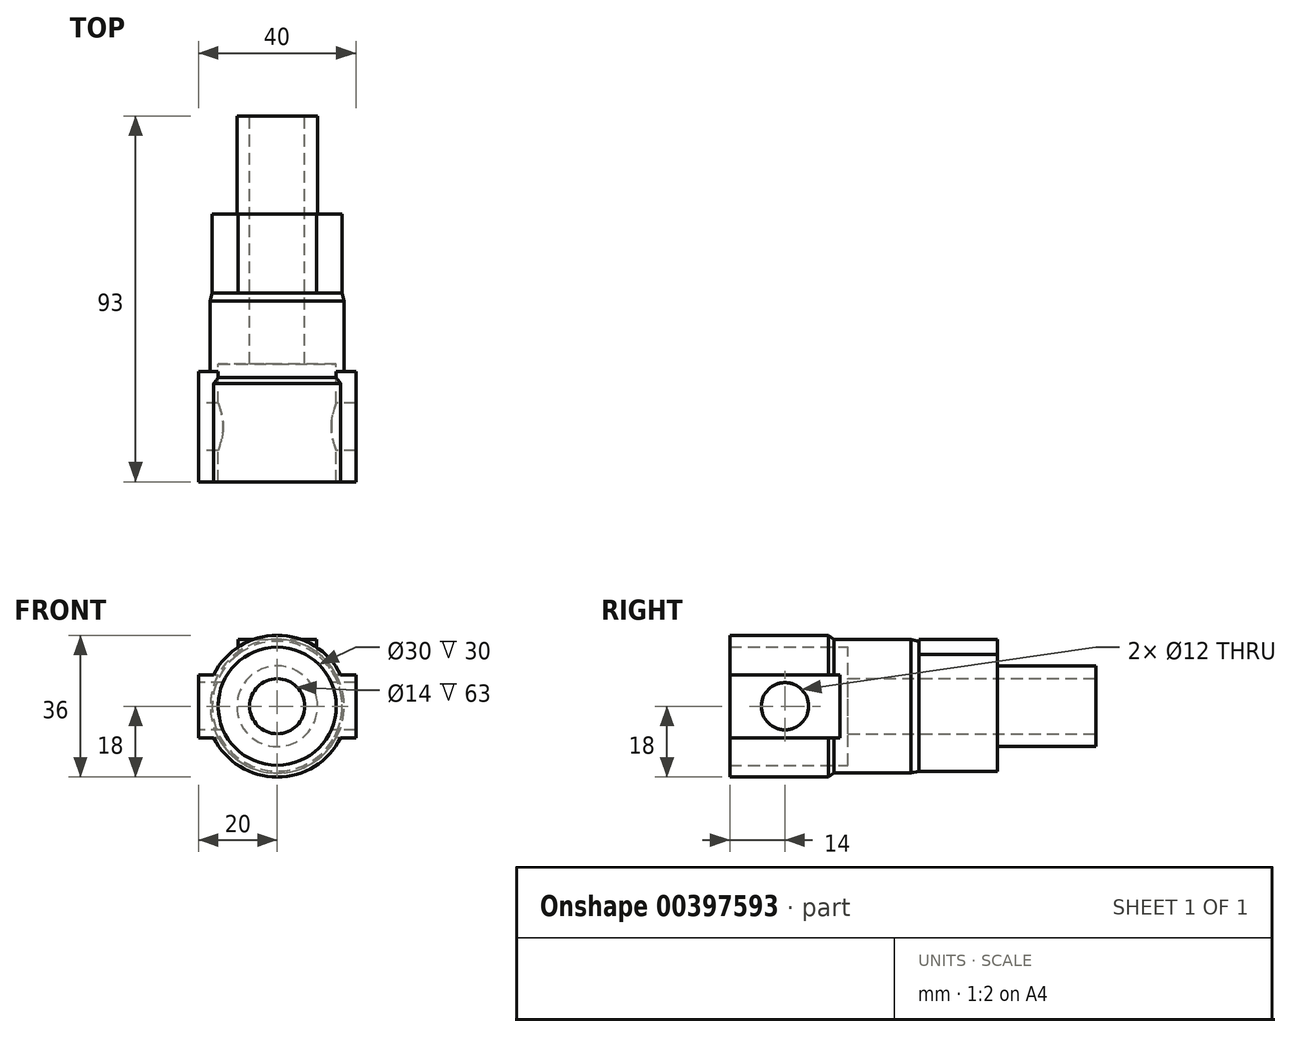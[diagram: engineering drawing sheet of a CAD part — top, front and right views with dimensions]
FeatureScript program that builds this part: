
annotation { "Feature Type Name" : "Feature", "Feature Type Description" : "" }
export const myFeature = defineFeature(function(context is Context, id is Id, definition is map)
    precondition{}
    {
        {
            var Q0;
            Q0=qCreatedBy(makeId("Front.planeOp"),FACE);
            var sketch = newSketch(context, id + "F0", { "sketchPlane" : qUnion([Q0])});
            skCircle(sketch, "E0", {"center": v(0, 0) * mm, "radius": 15 * mm});
            skCircle(sketch, "E1", {"center": v(0, 0) * mm, "radius": 18 * mm});
            skSolve(sketch);
        }
        {
            var Q0;
            Q0=qSketchRegion(id+"F0",true);
            extrude(context, id + "F1", {"entities" : qUnion([Q0]), "depth" : 28 * mm});
        }
        {
            var Q0;
            Q0=qCreatedBy(makeId("Right.planeOp"),FACE);
            var sketch = newSketch(context, id + "F2", { "sketchPlane" : qUnion([Q0])});
            skLineSegment(sketch, "E2", {"start": v(0, 0) * mm, "end": v(0, 8) * mm});
            skLineSegment(sketch, "E3", {"start": v(0, 0) * mm, "end": v(0, -8) * mm});
            skLineSegment(sketch, "E4.bottom", {"start": v(0, 8) * mm, "end": v(-28, 8) * mm});
            skLineSegment(sketch, "E4.top", {"start": v(0, -8) * mm, "end": v(-28, -8) * mm});
            skLineSegment(sketch, "E4.left", {"start": v(0, 8) * mm, "end": v(0, -8) * mm});
            skLineSegment(sketch, "E4.right", {"start": v(-28, 8) * mm, "end": v(-28, -8) * mm});
            skSolve(sketch);
        }
        {
            var Q0;
            Q0=qSketchRegion(id+"F2",true);
            extrude(context, id + "F3", {"entities" : qUnion([Q0]), "operationType" : NewBodyOperationType.ADD, "oppositeDirection" : true, "depth" : 20 * mm});
        }
        {
            var Q0;
            Q0=makeQuery(id+"F3.opExtrude","CAP_FACE",FACE,{"disambiguationData":[OSD([sQuery(id+"F2.wireOp",EDGE,"E4.bottom"),sQuery(id+"F2.wireOp",EDGE,"E4.top"),sQuery(id+"F2.wireOp",EDGE,"E4.left"),sQuery(id+"F2.wireOp",EDGE,"E4.right")])],"isStart":true});
            extrude(context, id + "F4", {"entities" : qUnion([Q0]), "operationType" : NewBodyOperationType.ADD, "depth" : 20 * mm});
        }
        {
            var Q0;
            Q0=makeQuery(id+"F1.opExtrude","CAP_FACE",FACE,{"disambiguationData":[OSD([sQuery(id+"F0.wireOp",EDGE,"E0"),sQuery(id+"F0.wireOp",EDGE,"E1")])],"isStart":false});
            var sketch = newSketch(context, id + "F5", { "sketchPlane" : qUnion([Q0])});
            skCircle(sketch, "E5", {"center": v(0, 0) * mm, "radius": 9 * mm});
            skSolve(sketch);
        }
        {
            var Q0;
            Q0=qSketchRegion(id+"F5",true);
            extrude(context, id + "F6", {"entities" : qUnion([Q0]), "operationType" : NewBodyOperationType.REMOVE, "oppositeDirection" : true, "depth" : 25 * mm});
        }
        {
            var Q0;
            Q0=makeQuery(id+"F3.boolean.opBoolean","MERGE",FACE,{"derivedFrom":[makeQuery(id+"F1.opExtrude","CAP_FACE",FACE,{"disambiguationData":[OSD([sQuery(id+"F0.wireOp",EDGE,"E0"),sQuery(id+"F0.wireOp",EDGE,"E1")])],"isStart":true}),makeQuery(id+"F3.opExtrude","SWEPT_FACE",FACE,{"disambiguationData":[OSD([sQuery(id+"F2.wireOp",EDGE,"E4.left")])]})]});
            var sketch = newSketch(context, id + "F7", { "sketchPlane" : qUnion([Q0])});
            skCircle(sketch, "E6", {"center": v(0, 0) * mm, "radius": 6.5 * mm});
            skCircle(sketch, "E7", {"center": v(0, 0) * mm, "radius": 17 * mm});
            skSolve(sketch);
        }
        {
            var Q0;
            Q0=qSketchRegion(id+"F7",true);
            extrude(context, id + "F8", {"entities" : qUnion([Q0]), "operationType" : NewBodyOperationType.ADD, "depth" : 20 * mm});
        }
        {
            var Q0;
            Q0=makeQuery(id+"F8.opExtrude","CAP_EDGE",EDGE,{"disambiguationData":[OSD([sQuery(id+"F7.wireOp",EDGE,"E7")])],"isStart":false});
            chamfer(context, id + "F9", {"entities" : qUnion([Q0]), "chamferType" : ChamferType.TWO_OFFSETS, "width1" : 0.5 * mm, "oppositeDirection" : false, "width2" : 2 * mm, "tangentPropagation" : true});
        }
        {
            var Q0;
            Q0=makeQuery(id+"F8.opExtrude","CAP_FACE",FACE,{"disambiguationData":[OSD([sQuery(id+"F7.wireOp",EDGE,"E6"),sQuery(id+"F7.wireOp",EDGE,"E7")])],"isStart":false});
            extrude(context, id + "F10", {"entities" : qUnion([Q0]), "operationType" : NewBodyOperationType.ADD, "depth" : 20 * mm});
        }
        {
            var Q0;
            Q0=qCreatedBy(makeId("Top.planeOp"),FACE);
            var sketch = newSketch(context, id + "F11", { "sketchPlane" : qUnion([Q0])});
            skLineSegment(sketch, "E8", {"start": v(0, 0) * mm, "end": v(0, 60) * mm});
            skLineSegment(sketch, "E9.bottom", {"start": v(-10, 40) * mm, "end": v(10, 40) * mm});
            skLineSegment(sketch, "E9.top", {"start": v(-10, 20) * mm, "end": v(10, 20) * mm});
            skLineSegment(sketch, "E9.left", {"start": v(-10, 40) * mm, "end": v(-10, 20) * mm});
            skLineSegment(sketch, "E9.right", {"start": v(10, 40) * mm, "end": v(10, 20) * mm});
            skPoint(sketch, "E9.middle", {"position": v(0, 30) * mm});
            skSolve(sketch);
        }
        {
            var Q0;
            Q0=qSketchRegion(id+"F11",true);
            extrude(context, id + "F12", {"entities" : qUnion([Q0]), "operationType" : NewBodyOperationType.ADD, "depth" : 17 * mm});
        }
        {
            var Q0;
            Q0=makeQuery(id+"F3.boolean.opBoolean","MERGE",FACE,{"derivedFrom":[makeQuery(id+"F1.opExtrude","CAP_FACE",FACE,{"disambiguationData":[OSD([sQuery(id+"F0.wireOp",EDGE,"E0"),sQuery(id+"F0.wireOp",EDGE,"E1")])],"isStart":false}),makeQuery(id+"F3.opExtrude","SWEPT_FACE",FACE,{"disambiguationData":[OSD([sQuery(id+"F2.wireOp",EDGE,"E4.right")])]})]});
            var sketch = newSketch(context, id + "F13", { "sketchPlane" : qUnion([Q0])});
            skCircle(sketch, "E10", {"center": v(0, 0) * mm, "radius": 15 * mm});
            skSolve(sketch);
        }
        {
            var Q0;
            Q0=qSketchRegion(id+"F13",true);
            extrude(context, id + "F14", {"entities" : qUnion([Q0]), "operationType" : NewBodyOperationType.REMOVE, "oppositeDirection" : true, "depth" : 30 * mm});
        }
        {
            var Q0;
            Q0=makeQuery(id+"F12.boolean.opBoolean","MERGE",FACE,{"derivedFrom":[makeQuery(id+"F10.opExtrude","CAP_FACE",FACE,{"disambiguationData":[OSD([sQuery(id+"F7.wireOp",EDGE,"E6"),sQuery(id+"F7.wireOp",EDGE,"E7")])],"isStart":false}),makeQuery(id+"F12.opExtrude","SWEPT_FACE",FACE,{"disambiguationData":[OSD([sQuery(id+"F11.wireOp",EDGE,"E9.bottom")])]})]});
            var sketch = newSketch(context, id + "F15", { "sketchPlane" : qUnion([Q0])});
            skCircle(sketch, "E11", {"center": v(0, 0) * mm, "radius": 7 * mm});
            skSolve(sketch);
        }
        {
            var Q0;
            Q0=makeQuery(id+"F15.imprint","IMPRINT",FACE,{"disambiguationData":[TD([[makeQuery(id+"F15.imprint","IMPRINT",EDGE,{"derivedFrom":sQuery(id+"F15.wireOp",EDGE,"E11")}),1.0]])]});
            extrude(context, id + "F16", {"entities" : qUnion([Q0]), "operationType" : NewBodyOperationType.REMOVE, "oppositeDirection" : true, "depth" : 200 * mm});
        }
        {
            var Q0;
            Q0=makeQuery(id+"F1.opExtrude","CAP_EDGE",EDGE,{"disambiguationData":[OSD([sQuery(id+"F0.wireOp",EDGE,"E1")])],"isStart":true});
            chamfer(context, id + "F17", {"entities" : qUnion([Q0]), "chamferType" : ChamferType.TWO_OFFSETS, "width1" : 3 * mm, "oppositeDirection" : false, "width2" : 2 * mm, "tangentPropagation" : true});
        }
        {
            var Q0;
            Q0=makeQuery(id+"F12.boolean.opBoolean","MERGE",FACE,{"derivedFrom":[makeQuery(id+"F10.opExtrude","CAP_FACE",FACE,{"disambiguationData":[OSD([sQuery(id+"F7.wireOp",EDGE,"E6"),sQuery(id+"F7.wireOp",EDGE,"E7")])],"isStart":false}),makeQuery(id+"F12.opExtrude","SWEPT_FACE",FACE,{"disambiguationData":[OSD([sQuery(id+"F11.wireOp",EDGE,"E9.bottom")])]})]});
            var sketch = newSketch(context, id + "F18", { "sketchPlane" : qUnion([Q0])});
            skCircle(sketch, "E12", {"center": v(0, 0) * mm, "radius": 10.25 * mm});
            skSolve(sketch);
        }
        {
            var Q0;
            Q0=makeQuery(id+"F18.imprint","IMPRINT",FACE,{"disambiguationData":[TD([[makeQuery(id+"F18.imprint","IMPRINT",EDGE,{"derivedFrom":sQuery(id+"F18.wireOp",EDGE,"E12")}),1.0]])]});
            extrude(context, id + "F19", {"entities" : qUnion([Q0]), "operationType" : NewBodyOperationType.ADD, "depth" : 25 * mm});
        }
        {
            var Q0;
            Q0=makeQuery(id+"F3.opExtrude","CAP_FACE",FACE,{"disambiguationData":[OSD([sQuery(id+"F2.wireOp",EDGE,"E4.bottom"),sQuery(id+"F2.wireOp",EDGE,"E4.top"),sQuery(id+"F2.wireOp",EDGE,"E4.left"),sQuery(id+"F2.wireOp",EDGE,"E4.right")])],"isStart":false});
            var sketch = newSketch(context, id + "F20", { "sketchPlane" : qUnion([Q0])});
            skCircle(sketch, "E13", {"center": v(14, 0) * mm, "radius": 6 * mm});
            skPoint(sketch, "E13.centerSnap0", {"position": v(14, 8) * mm});
            skPoint(sketch, "E13.centerSnap1", {"position": v(0, 0) * mm});
            skSolve(sketch);
        }
        {
            var Q0;
            Q0=makeQuery(id+"F20.imprint","IMPRINT",FACE,{"disambiguationData":[TD([[makeQuery(id+"F20.imprint","IMPRINT",EDGE,{"derivedFrom":sQuery(id+"F20.wireOp",EDGE,"E13")}),1.0]])]});
            extrude(context, id + "F21", {"entities" : qUnion([Q0]), "operationType" : NewBodyOperationType.REMOVE, "oppositeDirection" : true, "depth" : 45 * mm});
        }
    });
